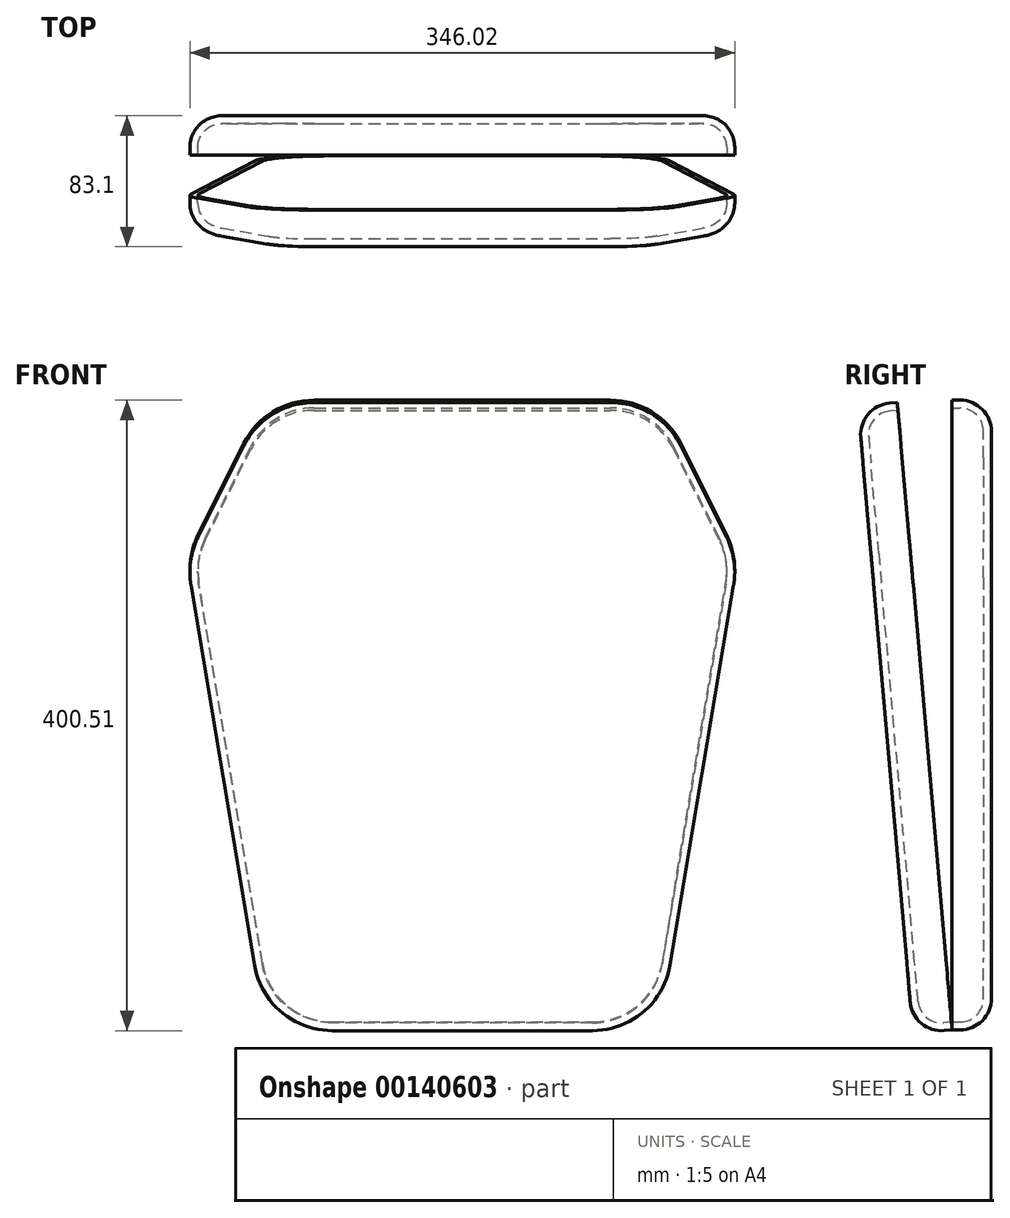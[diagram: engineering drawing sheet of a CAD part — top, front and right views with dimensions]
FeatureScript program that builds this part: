
annotation { "Feature Type Name" : "Feature", "Feature Type Description" : "" }
export const myFeature = defineFeature(function(context is Context, id is Id, definition is map)
    precondition{}
    {
        {
            var Q0;
            Q0=qCreatedBy(makeId("Front.planeOp"),FACE);
            var sketch = newSketch(context, id + "F0", { "sketchPlane" : qUnion([Q0])});
            skLineSegment(sketch, "E0.bottom", {"start": v(-125, -200) * mm, "end": v(125, -200) * mm});
            skLineSegment(sketch, "E0.top", {"start": v(-125, 200) * mm, "end": v(125, 200) * mm});
            skLineSegment(sketch, "E0.left", {"start": v(-125, -200) * mm, "end": v(-125, 200) * mm, "construction": true});
            skLineSegment(sketch, "E0.right", {"start": v(125, -200) * mm, "end": v(125, 200) * mm, "construction": true});
            skPoint(sketch, "E0.middle", {"position": v(0, 0) * mm});
            skLineSegment(sketch, "E1", {"start": v(-125, -200) * mm, "end": v(-175, 100) * mm});
            skLineSegment(sketch, "E2", {"start": v(-175, 100) * mm, "end": v(-125, 200) * mm});
            skLineSegment(sketch, "E3", {"start": v(125, -200) * mm, "end": v(175, 100) * mm});
            skLineSegment(sketch, "E4", {"start": v(175, 100) * mm, "end": v(125, 200) * mm});
            skLineSegment(sketch, "E5", {"start": v(-175, 100) * mm, "end": v(-125, 100) * mm, "construction": true});
            skLineSegment(sketch, "E6", {"start": v(175, 100) * mm, "end": v(125, 100) * mm, "construction": true});
            skSolve(sketch);
        }
        {
            var Q0;
            Q0 = qSketchRegion(id + "F0", true);
            extrude(context, id + "F1", {"entities" : qUnion([Q0]), "oppositeDirection" : true, "depth" : 25 * mm, "offsetDistance" : 25 * mm});
        }
        {
            var Q0;
            Q0=makeQuery(id+"F1.opExtrude","SWEPT_EDGE",EDGE,{"disambiguationData":[OSD([sQuery(id+"F0.wireOp",EDGE,"E0.bottom"),sQuery(id+"F0.wireOp",EDGE,"E3")])]});
            var Q1;
            Q1=makeQuery(id+"F1.opExtrude","SWEPT_EDGE",EDGE,{"disambiguationData":[OSD([sQuery(id+"F0.wireOp",EDGE,"E0.bottom"),sQuery(id+"F0.wireOp",EDGE,"E1")])]});
            var Q2;
            Q2=makeQuery(id+"F1.opExtrude","SWEPT_EDGE",EDGE,{"disambiguationData":[OSD([sQuery(id+"F0.wireOp",EDGE,"E0.top"),sQuery(id+"F0.wireOp",EDGE,"E2")])]});
            var Q3;
            Q3=makeQuery(id+"F1.opExtrude","SWEPT_EDGE",EDGE,{"disambiguationData":[OSD([sQuery(id+"F0.wireOp",EDGE,"E0.top"),sQuery(id+"F0.wireOp",EDGE,"E4")])]});
            var Q4;
            Q4=makeQuery(id+"F1.opExtrude","SWEPT_EDGE",EDGE,{"disambiguationData":[OSD([sQuery(id+"F0.wireOp",EDGE,"E3"),sQuery(id+"F0.wireOp",EDGE,"E4")])]});
            var Q5;
            Q5=makeQuery(id+"F1.opExtrude","SWEPT_EDGE",EDGE,{"disambiguationData":[OSD([sQuery(id+"F0.wireOp",EDGE,"E1"),sQuery(id+"F0.wireOp",EDGE,"E2")])]});
            fillet(context, id + "F2", {"entities" : qUnion([Q0, Q1, Q2, Q3, Q4, Q5]), "radius" : 50 * mm, "tangentPropagation" : true, "allowEdgeOverflow" : false});
        }
        {
            var Q0;
            Q0=makeQuery(id+"F1.opExtrude","CAP_FACE",FACE,{"disambiguationData":[OSD([sQuery(id+"F0.wireOp",EDGE,"E0.bottom"),sQuery(id+"F0.wireOp",EDGE,"E0.top"),sQuery(id+"F0.wireOp",EDGE,"E1"),sQuery(id+"F0.wireOp",EDGE,"E2"),sQuery(id+"F0.wireOp",EDGE,"E3"),sQuery(id+"F0.wireOp",EDGE,"E4")])],"isStart":false});
            fillet(context, id + "F3", {"entities" : qUnion([Q0]), "radius" : 20 * mm, "tangentPropagation" : true, "allowEdgeOverflow" : false});
        }
        {
            var Q0;
            Q0=makeQuery(id+"F1.opExtrude","CAP_FACE",FACE,{"disambiguationData":[OSD([sQuery(id+"F0.wireOp",EDGE,"E0.bottom"),sQuery(id+"F0.wireOp",EDGE,"E0.top"),sQuery(id+"F0.wireOp",EDGE,"E1"),sQuery(id+"F0.wireOp",EDGE,"E2"),sQuery(id+"F0.wireOp",EDGE,"E3"),sQuery(id+"F0.wireOp",EDGE,"E4")])],"isStart":true});
            shell(context, id + "F4", {"entities" : qUnion([Q0]), "thickness" : 5 * mm});
        }
        {
            var Q0;
            Q0=makeQuery(id+"F1.opExtrude","SWEPT_BODY",BODY,{"disambiguationData":[OSD([sQuery(id+"F0.wireOp",EDGE,"E0.bottom"),sQuery(id+"F0.wireOp",EDGE,"E0.top"),sQuery(id+"F0.wireOp",EDGE,"E1"),sQuery(id+"F0.wireOp",EDGE,"E2"),sQuery(id+"F0.wireOp",EDGE,"E3"),sQuery(id+"F0.wireOp",EDGE,"E4")])]});
            var Q1;
            Q1=qCreatedBy(makeId("Front.planeOp"),FACE);
            mirror(context, id + "F5", {"entities" : qUnion([Q0]), "mirrorPlane" : qUnion([Q1])});
        }
        {
            var Q0;
            Q0=makeQuery(id+"F5.opPattern","COPY",BODY,{"derivedFrom":makeQuery(id+"F1.opExtrude","SWEPT_BODY",BODY,{"disambiguationData":[OSD([sQuery(id+"F0.wireOp",EDGE,"E0.bottom"),sQuery(id+"F0.wireOp",EDGE,"E0.top"),sQuery(id+"F0.wireOp",EDGE,"E1"),sQuery(id+"F0.wireOp",EDGE,"E2"),sQuery(id+"F0.wireOp",EDGE,"E3"),sQuery(id+"F0.wireOp",EDGE,"E4")])]}),"instanceName":"1"});
            var Q1;
            Q1=makeQuery(id+"F1.opExtrude","CAP_EDGE",EDGE,{"disambiguationData":[OSD([sQuery(id+"F0.wireOp",EDGE,"E0.bottom")])],"isStart":true});
            transform(context, id + "F6", {"entities" : qUnion([Q0]), "transformType" : TransformType.ROTATION, "transformAxis" : qUnion([Q1]), "angle" : 5 * degree, "makeCopy" : false});
        }
    });
